# Revit family: Sink_Kitchen_Abey_Builders_SingleBowl_Overflow_Large_FaceBased
name_source: partatom
category: Plumbing Fixtures
units: mm (PartAtom-declared; Revit-internal decimal feet)

## family parameters
Cut with Voids When Loaded = Yes
Host = Face
Maintain Annotation Orientation = No
OmniClass Number = 23.31.13.00
OmniClass Title = Sinks
Part Type = Normal
Room Calculation Point = No
Round Connector Dimension = Use Diameter
Shared = No

## types (2) — shared parameters
Assembly Code = D2010410
BodyMaterial = Metal_Abey_StainlessSteel
CW Connection = No
Default Elevation = 900 mm
Description = Abey CUA Large Single Bowl Kitchen Sink
HW Connection = No
IfcExportAs = IfcSanitaryTerminal
IfcExportType = SINK
Manufacturer = Abey
ManufacturerOverallDepth = 440 mm
ManufacturerOverallHeight = 200 mm
ManufacturerURLProductSpecific = https://www.abeyspecifier.com.au
ModifiedIssue = 20251103 $
PopOutMaterial = Metal_Abey_StainlessSteel
URL = https://www.abey.com.au
Uniclass2015Code = Pr_40_20_96_45
Uniclass2015Title = Kitchen sinks
Uniclass2015Version = Products v1.38
Vent Connection = No
Waste Connection = Yes
zero-valued in all types: Cost

## per-type parameters (varying)
| type | ManufacturerOverallWidth | Type Comments |
| CUA500-12 | 540 mm | Sink - Kitchen - Single Bowl - Overflow - Large - Large Single Bowl Kitchen Sink |
| CUA720-12 | 720 mm | Sink - Kitchen - Single Bowl - Overflow - Large - 54.8 Litres Stainless Steel |

note: column(s) folded — value = type name in every type: ManufacturerSpecCode, Model

## geometry (parser evidence)
native form markers: Sweep x7
no freeform markers — native parametric forms only
